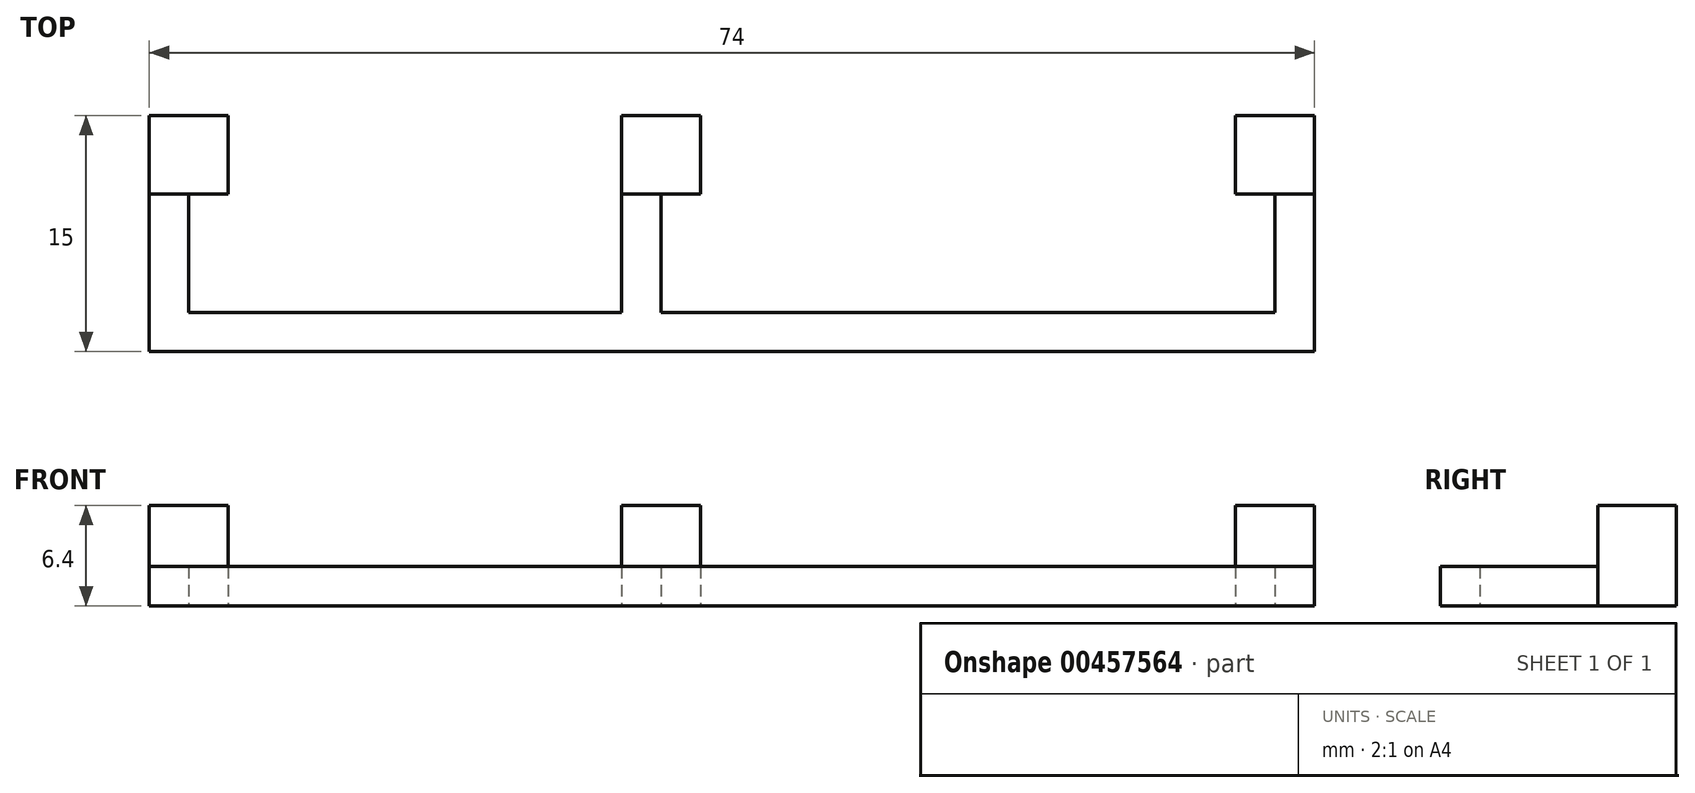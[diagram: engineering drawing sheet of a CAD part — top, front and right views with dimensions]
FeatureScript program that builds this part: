
annotation { "Feature Type Name" : "Feature", "Feature Type Description" : "" }
export const myFeature = defineFeature(function(context is Context, id is Id, definition is map)
    precondition{}
    {
        {
            var Q0;
            Q0=qCreatedBy(makeId("Top.planeOp"),FACE);
            var sketch = newSketch(context, id + "F0", { "sketchPlane" : qUnion([Q0])});
            skLineSegment(sketch, "E0.bottom", {"start": v(0, 0) * mm, "end": v(-5, 0) * mm});
            skLineSegment(sketch, "E0.top", {"start": v(0, 5) * mm, "end": v(-5, 5) * mm});
            skLineSegment(sketch, "E0.left", {"start": v(0, 0) * mm, "end": v(0, 5) * mm});
            skLineSegment(sketch, "E0.right", {"start": v(-5, 0) * mm, "end": v(-5, 5) * mm});
            skLineSegment(sketch, "E1", {"start": v(0, 0) * mm, "end": v(0, -10) * mm});
            skLineSegment(sketch, "E2", {"start": v(0, -10) * mm, "end": v(-74, -10) * mm});
            skLineSegment(sketch, "E3.top", {"start": v(-74, 5) * mm, "end": v(-69, 5) * mm});
            skLineSegment(sketch, "E3.right", {"start": v(-69, 0) * mm, "end": v(-69, 5) * mm});
            skLineSegment(sketch, "E4", {"start": v(-71.5, 0) * mm, "end": v(-71.5, -7.5) * mm, "construction": true});
            skLineSegment(sketch, "E5", {"start": v(-71.5, 0) * mm, "end": v(-71.5, -7.5) * mm});
            skLineSegment(sketch, "E6", {"start": v(-2.5, -7.5) * mm, "end": v(-2.5, 0) * mm});
            skLineSegment(sketch, "E7.bottom", {"start": v(-44, 0) * mm, "end": v(-39, 0) * mm});
            skLineSegment(sketch, "E7.top", {"start": v(-44, 5) * mm, "end": v(-39, 5) * mm});
            skLineSegment(sketch, "E7.left", {"start": v(-44, 0) * mm, "end": v(-44, 5) * mm});
            skLineSegment(sketch, "E7.right", {"start": v(-39, 0) * mm, "end": v(-39, 5) * mm});
            skLineSegment(sketch, "E8", {"start": v(-44, 0) * mm, "end": v(-44, -7.5) * mm});
            skLineSegment(sketch, "E9", {"start": v(-44, 0) * mm, "end": v(-41.5, 0) * mm, "construction": true});
            skLineSegment(sketch, "E10", {"start": v(-41.5, 0) * mm, "end": v(-41.5, -7.5) * mm, "construction": true});
            skLineSegment(sketch, "E11", {"start": v(-41.5, 0) * mm, "end": v(-41.5, -7.5) * mm});
            skLineSegment(sketch, "E12", {"start": v(-2.5, -7.5) * mm, "end": v(-41.5, -7.5) * mm});
            skLineSegment(sketch, "E13", {"start": v(-44, -7.5) * mm, "end": v(-71.5, -7.5) * mm});
            skLineSegment(sketch, "E14", {"start": v(-74, 5) * mm, "end": v(-74, -10) * mm});
            skLineSegment(sketch, "E15", {"start": v(-71.5, 0) * mm, "end": v(-74, 0) * mm});
            skLineSegment(sketch, "E16", {"start": v(-69, 0) * mm, "end": v(-71.5, 0) * mm});
            skSolve(sketch);
        }
        {
            var Q0;
            Q0=makeQuery(id+"F0.imprint","IMPRINT",FACE,{"disambiguationData":[TD([[makeQuery(id+"F0.imprint","IMPRINT",EDGE,{"derivedFrom":sQuery(id+"F0.wireOp",EDGE,"E0.top")}),1.0]])]});
            var Q1;
            Q1=makeQuery(id+"F0.imprint","IMPRINT",FACE,{"disambiguationData":[TD([[makeQuery(id+"F0.imprint","IMPRINT",EDGE,{"derivedFrom":sQuery(id+"F0.wireOp",EDGE,"E3.top")}),-1.0]])]});
            var Q2;
            Q2=makeQuery(id+"F0.imprint","IMPRINT",FACE,{"disambiguationData":[TD([[makeQuery(id+"F0.imprint","IMPRINT",EDGE,{"derivedFrom":sQuery(id+"F0.wireOp",EDGE,"E7.top")}),-1.0]])]});
            extrude(context, id + "F1", {"entities" : qUnion([Q0, Q1, Q2]), "depth" : 6.4 * mm});
        }
        {
            var Q0;
            {var subQ7=sQuery(id+"F0.wireOp",EDGE,"E1");Q0=makeQuery(id+"F0.imprint","IMPRINT",FACE,{"disambiguationData":[TD([[makeQuery(id+"F0.imprint","IMPRINT",EDGE,{"derivedFrom":subQ7}),-1.0]])]});}
            extrude(context, id + "F2", {"entities" : qUnion([Q0]), "depth" : 2.5 * mm});
        }
    });
